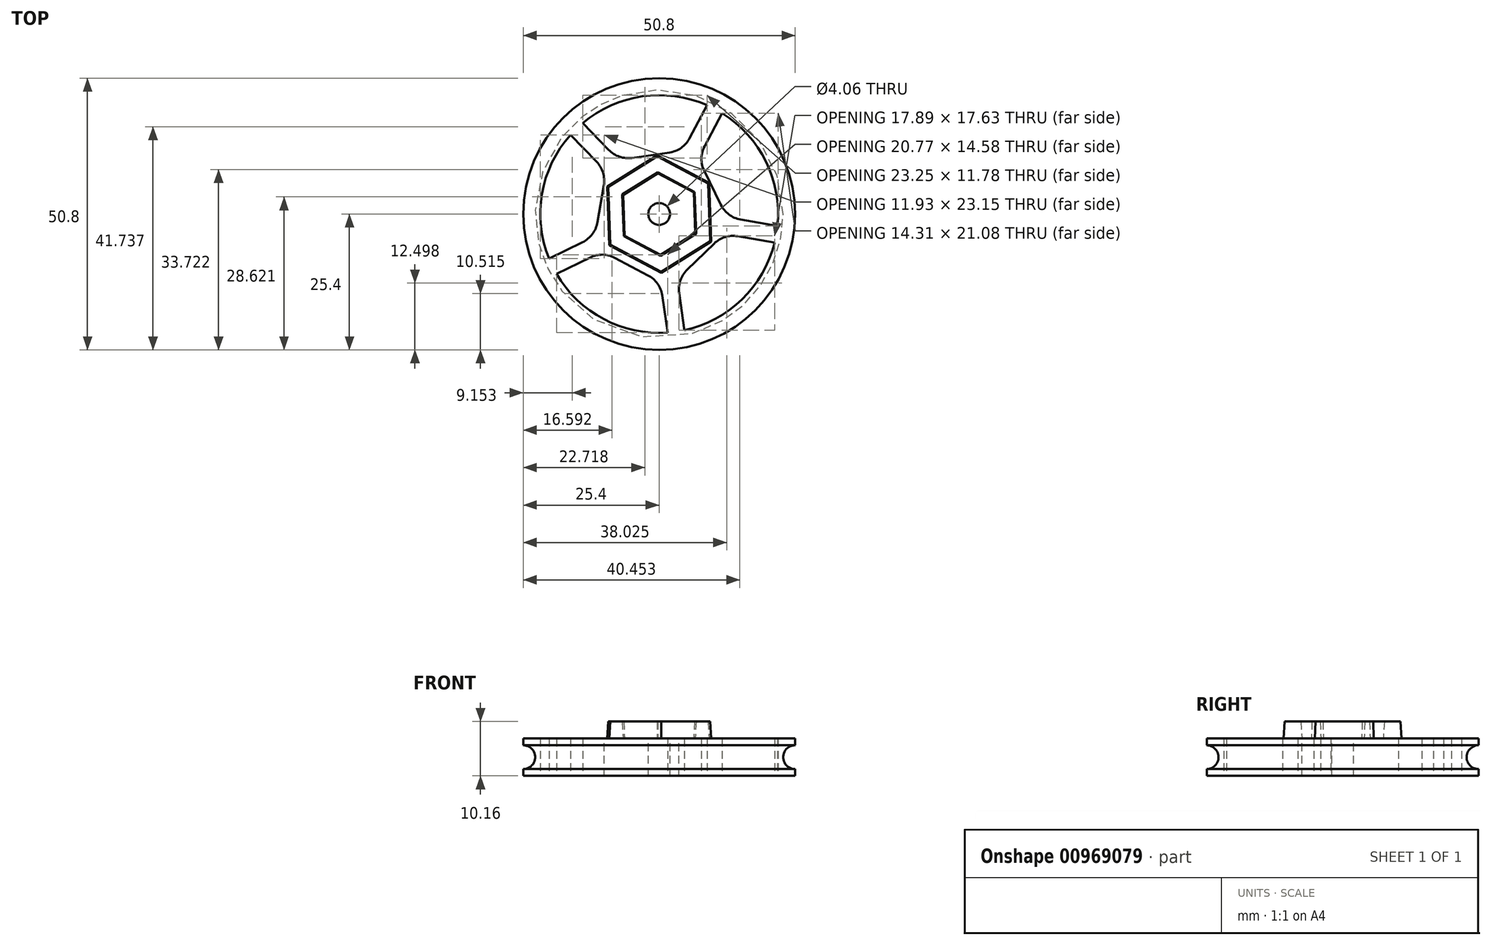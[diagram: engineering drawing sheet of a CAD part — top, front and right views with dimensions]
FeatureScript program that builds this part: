
annotation { "Feature Type Name" : "Feature", "Feature Type Description" : "" }
export const myFeature = defineFeature(function(context is Context, id is Id, definition is map)
    precondition{}
    {
        {
            var Q0;
            Q0=qCreatedBy(makeId("Right.planeOp"),FACE);
            var sketch = newSketch(context, id + "F0", { "sketchPlane" : qUnion([Q0])});
            skLineSegment(sketch, "E0", {"start": v(0, 0) * mm, "end": v(25.4, 0) * mm});
            skLineSegment(sketch, "E1", {"start": v(25.4, 6.99) * mm, "end": v(0, 6.98) * mm});
            skLineSegment(sketch, "E2", {"start": v(25.4, 6.99) * mm, "end": v(25.4, 5.72) * mm});
            skLineSegment(sketch, "E3", {"start": v(25.4, 0) * mm, "end": v(25.4, 1.27) * mm});
            skArc(sketch, "E4", {"start": v(25.4, 5.71) * mm, "mid": v(23.18, 3.5) * mm, "end": v(25.4, 1.27) * mm});
            skLineSegment(sketch, "E5", {"start": v(0, 6.98) * mm, "end": v(0, 0) * mm});
            skSolve(sketch);
        }
        {
            var Q0;
            Q0=makeQuery(id+"F0.imprint","IMPRINT",FACE,{"disambiguationData":[TD([[makeQuery(id+"F0.imprint","IMPRINT",EDGE,{"derivedFrom":sQuery(id+"F0.wireOp",EDGE,"E0")}),1.0]])]});
            var Q1;
            Q1=sQuery(id+"F0.wireOp",EDGE,"E5");
            revolve(context, id + "F1", {"surfaceOperationType" : NewSurfaceOperationType.NEW, "entities" : qUnion([Q0]), "axis" : qUnion([Q1]), "revolveType" : RevolveType.FULL});
        }
        {
            var Q0;
            Q0=makeQuery(id+"F1.opRevolve","SWEPT_FACE",FACE,{"disambiguationData":[OSD([sQuery(id+"F0.wireOp",EDGE,"E0")])]});
            var sketch = newSketch(context, id + "F2", { "sketchPlane" : qUnion([Q0])});
            skCircle(sketch, "E6.cCircle", {"center": v(0, 0) * mm, "radius": 22.23 * mm});
            skLineSegment(sketch, "E6.0", {"start": v(21.9, 3.8) * mm, "end": v(10.38, -19.65) * mm, "construction": true});
            skLineSegment(sketch, "E6.1", {"start": v(10.38, -19.65) * mm, "end": v(-15.49, -15.94) * mm, "construction": true});
            skLineSegment(sketch, "E6.2", {"start": v(-15.49, -15.94) * mm, "end": v(-19.95, 9.8) * mm, "construction": true});
            skLineSegment(sketch, "E6.3", {"start": v(-19.95, 9.8) * mm, "end": v(3.16, 22) * mm, "construction": true});
            skLineSegment(sketch, "E6.4", {"start": v(3.16, 22) * mm, "end": v(21.9, 3.8) * mm, "construction": true});
            skLineSegment(sketch, "E7", {"start": v(3.16, 22) * mm, "end": v(0, 0) * mm, "construction": true});
            skLineSegment(sketch, "E8", {"start": v(21.9, 3.8) * mm, "end": v(0, 0) * mm, "construction": true});
            skLineSegment(sketch, "E9", {"start": v(10.38, -19.65) * mm, "end": v(0, 0) * mm, "construction": true});
            skLineSegment(sketch, "E10", {"start": v(-15.49, -15.94) * mm, "end": v(0, 0) * mm, "construction": true});
            skLineSegment(sketch, "E11", {"start": v(-19.95, 9.8) * mm, "end": v(0, 0) * mm, "construction": true});
            skLineSegment(sketch, "E12", {"start": v(1.58, 22.17) * mm, "end": v(0.22, 12.68) * mm});
            skPoint(sketch, "E12.startSnap0", {"position": v(1.58, 11) * mm});
            skLineSegment(sketch, "E13", {"start": v(4.72, 21.72) * mm, "end": v(3.36, 12.23) * mm});
            skLineSegment(sketch, "E14", {"start": v(-19.2, 11.2) * mm, "end": v(-10.6, 6.97) * mm});
            skLineSegment(sketch, "E15", {"start": v(-20.6, 8.35) * mm, "end": v(-12, 4.12) * mm});
            skLineSegment(sketch, "E16", {"start": v(-14.3, -17) * mm, "end": v(-7.63, -10.13) * mm});
            skLineSegment(sketch, "E17", {"start": v(-16.59, -14.8) * mm, "end": v(-9.9, -7.92) * mm});
            skLineSegment(sketch, "E18", {"start": v(8.94, -20.35) * mm, "end": v(4.47, -11.87) * mm});
            skLineSegment(sketch, "E19", {"start": v(11.75, -18.86) * mm, "end": v(7.28, -10.39) * mm});
            skLineSegment(sketch, "E20", {"start": v(12.67, 0.58) * mm, "end": v(22.11, 2.22) * mm});
            skLineSegment(sketch, "E21", {"start": v(21.57, 5.35) * mm, "end": v(12.13, 3.71) * mm});
            skCircle(sketch, "E22.cCircle", {"center": v(0, 0) * mm, "radius": 11.11 * mm, "construction": true});
            skLineSegment(sketch, "E22.0", {"start": v(1.95, 13.6) * mm, "end": v(13.53, 2.34) * mm});
            skLineSegment(sketch, "E22.1", {"start": v(13.53, 2.34) * mm, "end": v(6.41, -12.15) * mm});
            skLineSegment(sketch, "E22.2", {"start": v(6.41, -12.15) * mm, "end": v(-9.57, -9.85) * mm});
            skLineSegment(sketch, "E22.3", {"start": v(-9.57, -9.85) * mm, "end": v(-12.33, 6.06) * mm});
            skLineSegment(sketch, "E22.4", {"start": v(-12.33, 6.06) * mm, "end": v(1.95, 13.6) * mm});
            skPoint(sketch, "E23", {"position": v(13.53, 2.34) * mm});
            skPoint(sketch, "E24", {"position": v(1.95, 13.6) * mm});
            skSolve(sketch);
        }
        {
            var Q0;
            {var subQ0=sQuery(id+"F2.wireOp",EDGE,"E12");Q0=makeQuery(id+"F2.imprint","IMPRINT",FACE,{"disambiguationData":[TD([[makeQuery(id+"F2.imprint","IMPRINT",EDGE,{"derivedFrom":subQ0}),-1.0]])]});}
            var Q1;
            {var subQ0=sQuery(id+"F2.wireOp",EDGE,"E13");Q1=makeQuery(id+"F2.imprint","IMPRINT",FACE,{"disambiguationData":[TD([[makeQuery(id+"F2.imprint","IMPRINT",EDGE,{"derivedFrom":subQ0}),1.0]])]});}
            var Q2;
            {var subQ0=sQuery(id+"F2.wireOp",EDGE,"E19");Q2=makeQuery(id+"F2.imprint","IMPRINT",FACE,{"disambiguationData":[TD([[makeQuery(id+"F2.imprint","IMPRINT",EDGE,{"derivedFrom":subQ0}),-1.0]])]});}
            var Q3;
            {var subQ0=sQuery(id+"F2.wireOp",EDGE,"E16");Q3=makeQuery(id+"F2.imprint","IMPRINT",FACE,{"disambiguationData":[TD([[makeQuery(id+"F2.imprint","IMPRINT",EDGE,{"derivedFrom":subQ0}),-1.0]])]});}
            var Q4;
            {var subQ0=sQuery(id+"F2.wireOp",EDGE,"E15");Q4=makeQuery(id+"F2.imprint","IMPRINT",FACE,{"disambiguationData":[TD([[makeQuery(id+"F2.imprint","IMPRINT",EDGE,{"derivedFrom":subQ0}),-1.0]])]});}
            extrude(context, id + "F3", {"entities" : qUnion([Q0, Q1, Q2, Q3, Q4]), "operationType" : NewBodyOperationType.REMOVE, "endBound" : BoundingType.THROUGH_ALL, "oppositeDirection" : true, "depth" : 25.4 * mm, "offsetDistance" : 25.4 * mm});
        }
        {
            var Q0;
            Q0=makeQuery(id+"F1.opRevolve","SWEPT_FACE",FACE,{"disambiguationData":[OSD([sQuery(id+"F0.wireOp",EDGE,"E1")])]});
            var sketch = newSketch(context, id + "F4", { "sketchPlane" : qUnion([Q0])});
            skCircle(sketch, "E25.cCircle", {"center": v(0, 0) * mm, "radius": 6.6 * mm, "construction": true});
            skLineSegment(sketch, "E25.0", {"start": v(-0.27, 7.62) * mm, "end": v(6.46, 4.05) * mm});
            skLineSegment(sketch, "E25.1", {"start": v(6.46, 4.05) * mm, "end": v(6.74, -3.58) * mm});
            skLineSegment(sketch, "E25.2", {"start": v(6.74, -3.58) * mm, "end": v(0.27, -7.62) * mm});
            skLineSegment(sketch, "E25.3", {"start": v(0.27, -7.62) * mm, "end": v(-6.46, -4.05) * mm});
            skLineSegment(sketch, "E25.4", {"start": v(-6.46, -4.05) * mm, "end": v(-6.74, 3.58) * mm});
            skLineSegment(sketch, "E25.5", {"start": v(-6.74, 3.58) * mm, "end": v(-0.27, 7.62) * mm});
            skPoint(sketch, "E25.0.midPoint", {"position": v(3.1, 5.83) * mm});
            skCircle(sketch, "E26.cCircle", {"center": v(0, 0) * mm, "radius": 9.53 * mm, "construction": true});
            skLineSegment(sketch, "E26.0", {"start": v(9.32, 5.83) * mm, "end": v(9.71, -5.16) * mm});
            skLineSegment(sketch, "E26.1", {"start": v(9.71, -5.16) * mm, "end": v(0.4, -11) * mm});
            skLineSegment(sketch, "E26.2", {"start": v(0.4, -11) * mm, "end": v(-9.32, -5.83) * mm});
            skLineSegment(sketch, "E26.3", {"start": v(-9.32, -5.83) * mm, "end": v(-9.71, 5.16) * mm});
            skLineSegment(sketch, "E26.4", {"start": v(-9.71, 5.16) * mm, "end": v(-0.4, 11) * mm});
            skLineSegment(sketch, "E26.5", {"start": v(-0.4, 11) * mm, "end": v(9.32, 5.83) * mm});
            skPoint(sketch, "E26.0.midPoint", {"position": v(9.52, 0.34) * mm});
            skSolve(sketch);
        }
        {
            var Q0;
            Q0 = qSketchRegion(id + "F4", true);
            extrude(context, id + "F5", {"entities" : qUnion([Q0]), "operationType" : NewBodyOperationType.ADD, "depth" : 3.17 * mm, "offsetDistance" : 25.4 * mm, "hasDraft" : true, "draftAngle" : 3 * degree, "draftPullDirection" : true});
        }
        {
            var Q0;
            Q0=makeQuery(id+"F5.boolean.opBoolean","SPLIT",FACE,{"disambiguationData":[TD([makeQuery(id+"F5.opExtrude","SWEPT_FACE",FACE,{"disambiguationData":[OSD([sQuery(id+"F4.wireOp",EDGE,"E25.0")])]})])],"derivedFrom":makeQuery(id+"F1.opRevolve","SWEPT_FACE",FACE,{"disambiguationData":[OSD([sQuery(id+"F0.wireOp",EDGE,"E1")])]})});
            var sketch = newSketch(context, id + "F6", { "sketchPlane" : qUnion([Q0])});
            skPoint(sketch, "E27", {"position": v(0, 0) * mm});
            skSolve(sketch);
        }
        {
            var Q0;
            Q0=sQuery(id+"F6.wireOp",VERTEX,"E27");
            var Q1;
            Q1=makeQuery(id+"F1.opRevolve","SWEPT_BODY",BODY,{"disambiguationData":[OSD([sQuery(id+"F0.wireOp",EDGE,"E0"),sQuery(id+"F0.wireOp",EDGE,"E1"),sQuery(id+"F0.wireOp",EDGE,"E2"),sQuery(id+"F0.wireOp",EDGE,"E3"),sQuery(id+"F0.wireOp",EDGE,"E4"),sQuery(id+"F0.wireOp",EDGE,"E5")])]});
            hole(context, id + "F7", {"style" : HoleStyle.SIMPLE, "endStyle" : HoleEndStyle.THROUGH, "holeDiameter" : 4.06 * mm, "majorDiameter" : 6.35 * mm, "isTappedThrough" : true, "tappedDepth" : 12.7 * mm, "tapClearance" : 3, "locations" : qUnion([Q0]), "scope" : qUnion([Q1])});
        }
        {
            var Q0;
            Q0=makeQuery(id+"F3.boolean.opBoolean","COPY",EDGE,{"derivedFrom":makeQuery(id+"F3.opExtrude","SWEPT_EDGE",EDGE,{"disambiguationData":[OSD([sQuery(id+"F2.wireOp",EDGE,"E15"),sQuery(id+"F2.wireOp",EDGE,"E22.3")])]})});
            var Q1;
            Q1=makeQuery(id+"F3.boolean.opBoolean","COPY",EDGE,{"derivedFrom":makeQuery(id+"F3.opExtrude","SWEPT_EDGE",EDGE,{"disambiguationData":[OSD([sQuery(id+"F2.wireOp",EDGE,"E17"),sQuery(id+"F2.wireOp",EDGE,"E22.3")])]})});
            var Q2;
            Q2=makeQuery(id+"F3.boolean.opBoolean","COPY",EDGE,{"derivedFrom":makeQuery(id+"F3.opExtrude","SWEPT_EDGE",EDGE,{"disambiguationData":[OSD([sQuery(id+"F2.wireOp",EDGE,"E18"),sQuery(id+"F2.wireOp",EDGE,"E22.2")])]})});
            var Q3;
            Q3=makeQuery(id+"F3.boolean.opBoolean","COPY",EDGE,{"derivedFrom":makeQuery(id+"F3.opExtrude","SWEPT_EDGE",EDGE,{"disambiguationData":[OSD([sQuery(id+"F2.wireOp",EDGE,"E12"),sQuery(id+"F2.wireOp",EDGE,"E22.4")])]})});
            var Q4;
            Q4=makeQuery(id+"F3.boolean.opBoolean","COPY",EDGE,{"derivedFrom":makeQuery(id+"F3.opExtrude","SWEPT_EDGE",EDGE,{"disambiguationData":[OSD([sQuery(id+"F2.wireOp",EDGE,"E19"),sQuery(id+"F2.wireOp",EDGE,"E22.1")])]})});
            var Q5;
            Q5=makeQuery(id+"F3.boolean.opBoolean","COPY",EDGE,{"derivedFrom":makeQuery(id+"F3.opExtrude","SWEPT_EDGE",EDGE,{"disambiguationData":[OSD([sQuery(id+"F2.wireOp",EDGE,"E20"),sQuery(id+"F2.wireOp",EDGE,"E22.1")])]})});
            var Q6;
            Q6=makeQuery(id+"F3.boolean.opBoolean","COPY",EDGE,{"derivedFrom":makeQuery(id+"F3.opExtrude","SWEPT_EDGE",EDGE,{"disambiguationData":[OSD([sQuery(id+"F2.wireOp",EDGE,"E13"),sQuery(id+"F2.wireOp",EDGE,"E22.0")])]})});
            var Q7;
            Q7=makeQuery(id+"F3.boolean.opBoolean","COPY",EDGE,{"derivedFrom":makeQuery(id+"F3.opExtrude","SWEPT_EDGE",EDGE,{"disambiguationData":[OSD([sQuery(id+"F2.wireOp",EDGE,"E21"),sQuery(id+"F2.wireOp",EDGE,"E22.0")])]})});
            var Q8;
            Q8=makeQuery(id+"F3.boolean.opBoolean","COPY",EDGE,{"derivedFrom":makeQuery(id+"F3.opExtrude","SWEPT_EDGE",EDGE,{"disambiguationData":[OSD([sQuery(id+"F2.wireOp",EDGE,"E16"),sQuery(id+"F2.wireOp",EDGE,"E22.2")])]})});
            var Q9;
            Q9=makeQuery(id+"F3.boolean.opBoolean","COPY",EDGE,{"derivedFrom":makeQuery(id+"F3.opExtrude","SWEPT_EDGE",EDGE,{"disambiguationData":[OSD([sQuery(id+"F2.wireOp",EDGE,"E14"),sQuery(id+"F2.wireOp",EDGE,"E22.4")])]})});
            fillet(context, id + "F8", {"entities" : qUnion([Q0, Q1, Q2, Q3, Q4, Q5, Q6, Q7, Q8, Q9]), "radius" : 5.08 * mm, "tangentPropagation" : true, "allowEdgeOverflow" : false});
        }
    });
